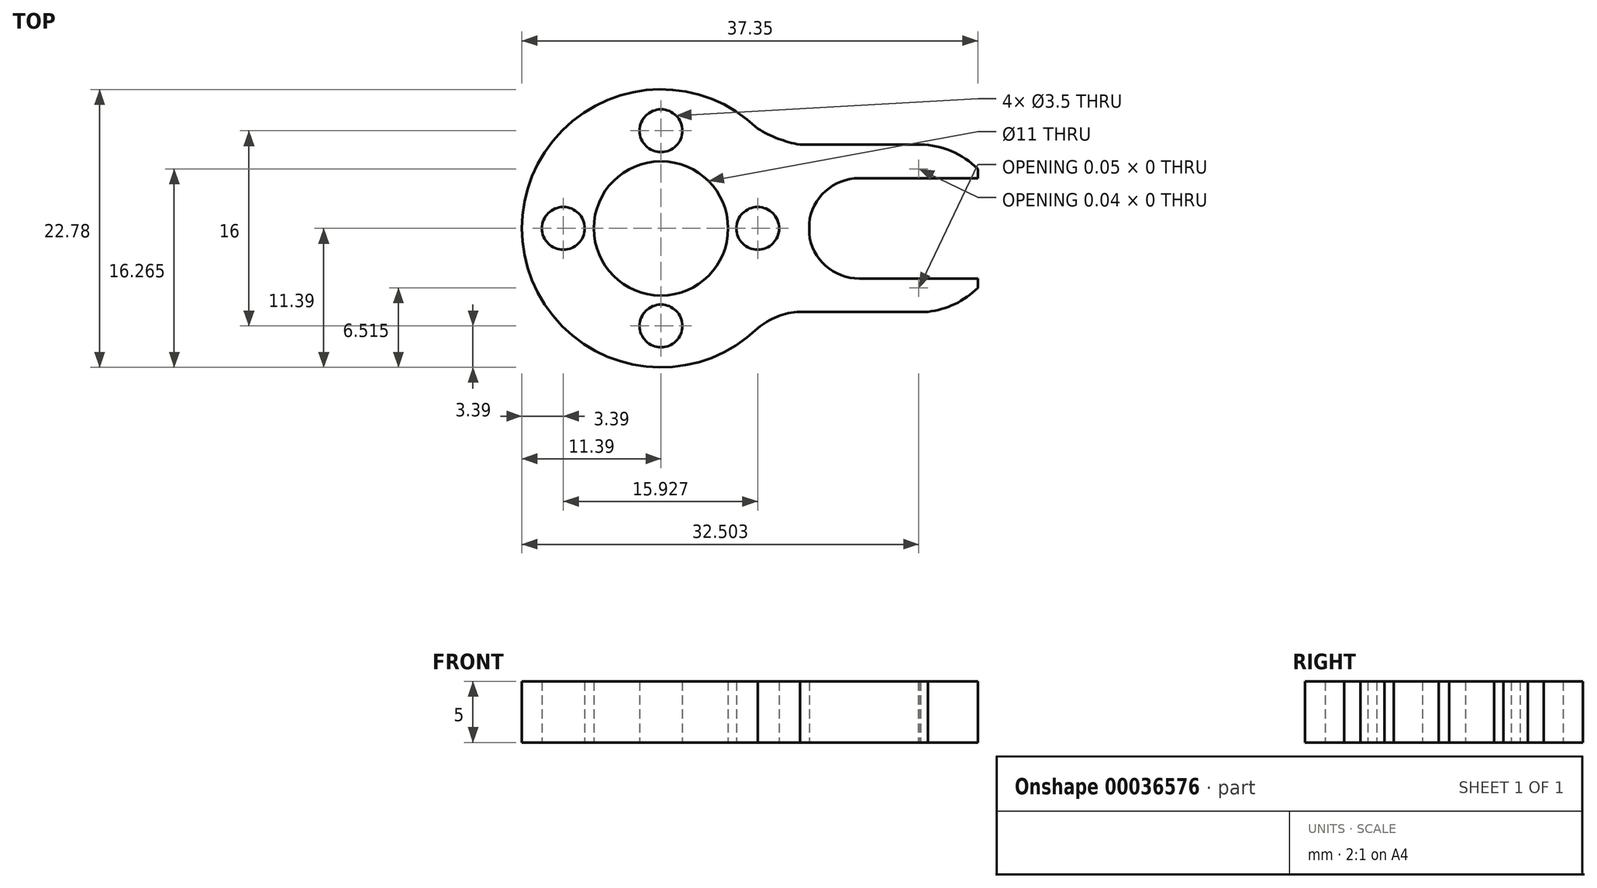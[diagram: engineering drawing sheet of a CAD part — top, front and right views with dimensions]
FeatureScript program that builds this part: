
annotation { "Feature Type Name" : "Feature", "Feature Type Description" : "" }
export const myFeature = defineFeature(function(context is Context, id is Id, definition is map)
    precondition{}
    {
        {
            var Q0;
            Q0=qCreatedBy(makeId("Top.planeOp"),FACE);
            var sketch = newSketch(context, id + "F0", { "sketchPlane" : qUnion([Q0])});
            skArc(sketch, "E0", {"start": v(7.93, 8.18) * mm, "mid": v(-11.4, 0) * mm, "end": v(7.93, -8.18) * mm});
            skCircle(sketch, "E1", {"center": v(0, 0) * mm, "radius": 5.5 * mm});
            skCircle(sketch, "E2", {"center": v(0, 8) * mm, "radius": 1.75 * mm});
            skCircle(sketch, "E3", {"center": v(-8, 0) * mm, "radius": 1.75 * mm});
            skCircle(sketch, "E4", {"center": v(0, -8) * mm, "radius": 1.75 * mm});
            skCircle(sketch, "E5", {"center": v(7.93, 0) * mm, "radius": 1.75 * mm});
            skArc(sketch, "E6", {"start": v(16.24, 4.87) * mm, "mid": v(12.95, 3.6) * mm, "end": v(11.38, 0.45) * mm});
            skArc(sketch, "E7", {"start": v(21.09, -4.87) * mm, "mid": v(21.11, -4.88) * mm, "end": v(21.14, -4.87) * mm});
            skArc(sketch, "E8", {"start": v(21.86, -6.83) * mm, "mid": v(24.08, -6.2) * mm, "end": v(25.96, -4.87) * mm});
            skLineSegment(sketch, "E9", {"start": v(21.26, 6.87) * mm, "end": v(11.38, 6.86) * mm});
            skLineSegment(sketch, "E10", {"start": v(21.86, -6.83) * mm, "end": v(11.38, -6.83) * mm});
            skLineSegment(sketch, "E11", {"start": v(16.26, -4.87) * mm, "end": v(25.96, -4.87) * mm});
            skLineSegment(sketch, "E12", {"start": v(25.96, 4.87) * mm, "end": v(16.24, 4.87) * mm});
            skLineSegment(sketch, "E13.trimOffspring", {"start": v(21.09, -4.87) * mm, "end": v(21.09, -4.87) * mm});
            skArc(sketch, "E14.trimOffspring", {"start": v(11.38, -0.45) * mm, "mid": v(12.96, -3.61) * mm, "end": v(16.26, -4.87) * mm});
            skArc(sketch, "E15.trimOffspring", {"start": v(25.96, 4.87) * mm, "mid": v(23.66, 6.39) * mm, "end": v(20.95, 6.87) * mm});
            skArc(sketch, "E16.trimOffspring", {"start": v(21.13, 4.87) * mm, "mid": v(21.1, 4.87) * mm, "end": v(21.07, 4.87) * mm});
            skArc(sketch, "E17", {"start": v(7.93, 8.18) * mm, "mid": v(9.6, 7.36) * mm, "end": v(11.38, 6.86) * mm});
            skArc(sketch, "E18", {"start": v(11.38, -6.83) * mm, "mid": v(9.55, -7.23) * mm, "end": v(7.93, -8.18) * mm});
            skArc(sketch, "E19.trimOffspring", {"start": v(11.38, -0.45) * mm, "mid": v(11.4, 0) * mm, "end": v(11.38, 0.45) * mm});
            skLineSegment(sketch, "E20.0", {"start": v(16.26, -4.11) * mm, "end": v(25.96, -4.11) * mm});
            skLineSegment(sketch, "E20.1", {"start": v(25.96, 4.11) * mm, "end": v(16.24, 4.11) * mm});
            skArc(sketch, "E20.2", {"start": v(16.24, 4.11) * mm, "mid": v(13.48, 3.06) * mm, "end": v(12.14, 0.43) * mm});
            skArc(sketch, "E20.3", {"start": v(12.14, -0.43) * mm, "mid": v(12.15, 0) * mm, "end": v(12.14, 0.43) * mm});
            skArc(sketch, "E20.4", {"start": v(12.14, -0.43) * mm, "mid": v(13.5, -3.07) * mm, "end": v(16.26, -4.11) * mm});
            skLineSegment(sketch, "E21", {"start": v(25.96, 4.87) * mm, "end": v(25.96, 4.11) * mm});
            skLineSegment(sketch, "E22", {"start": v(25.96, -4.87) * mm, "end": v(25.96, -4.11) * mm});
            skSolve(sketch);
        }
        {
            var Q0;
            Q0=makeQuery(id+"F0.imprint","IMPRINT",FACE,{"disambiguationData":[TD([[makeQuery(id+"F0.imprint","IMPRINT",EDGE,{"derivedFrom":sQuery(id+"F0.wireOp",EDGE,"E0")}),1.0]])]});
            var Q1;
            {var subQ9=sQuery(id+"F0.wireOp",EDGE,"E6");Q1=makeQuery(id+"F0.imprint","IMPRINT",FACE,{"disambiguationData":[TD([[makeQuery(id+"F0.imprint","IMPRINT",EDGE,{"derivedFrom":subQ9}),1.0]])]});}
            extrude(context, id + "F1", {"entities" : qUnion([Q0, Q1]), "depth" : 5 * mm});
        }
    });
